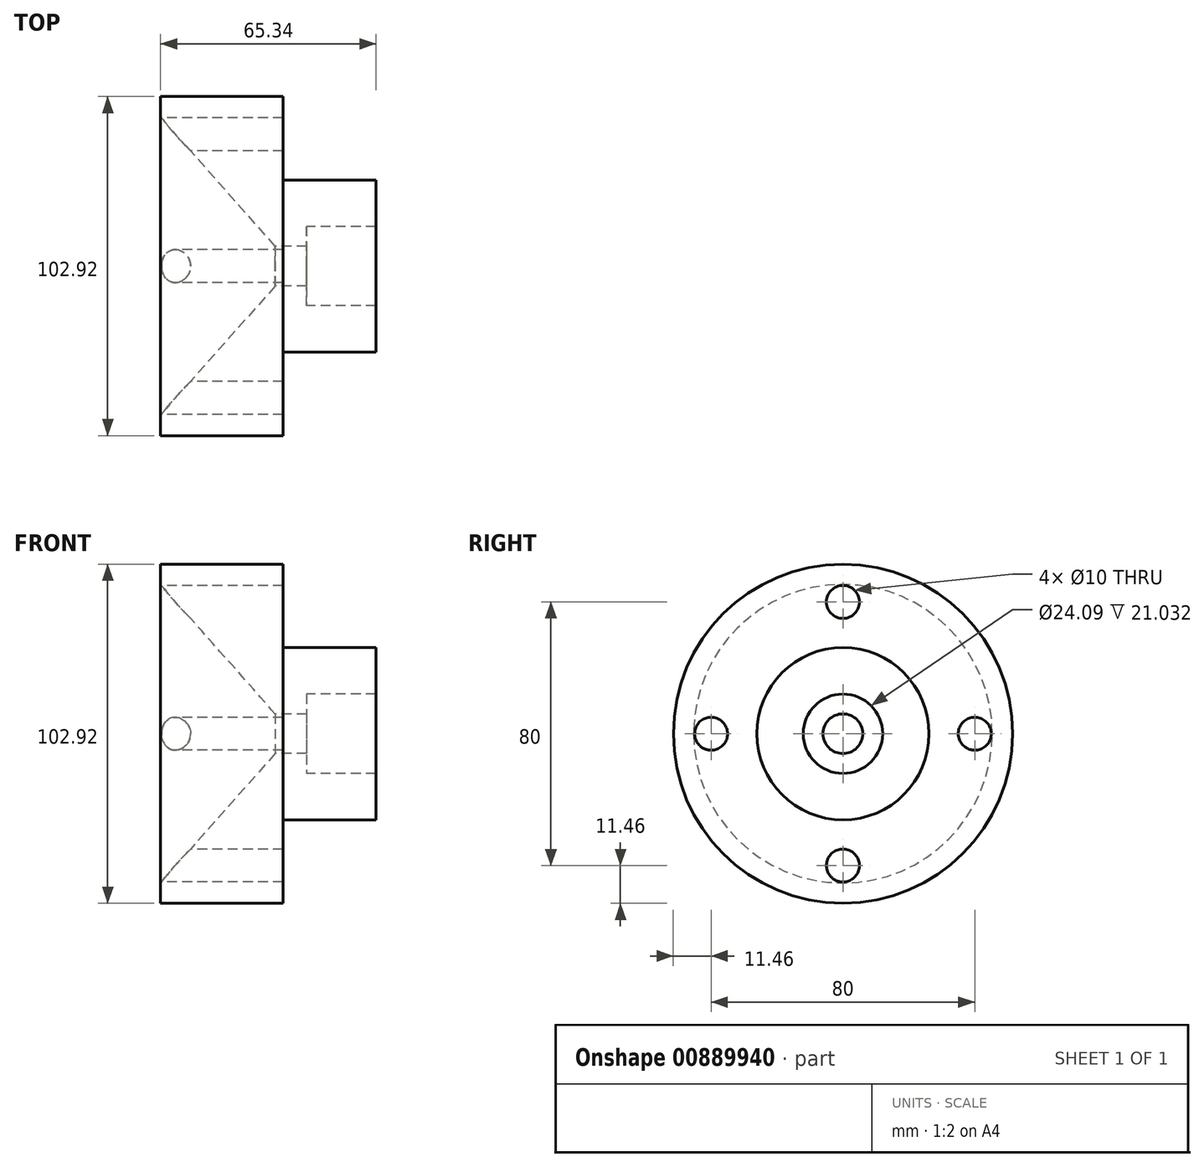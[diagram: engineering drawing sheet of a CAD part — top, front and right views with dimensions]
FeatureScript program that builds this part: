
annotation { "Feature Type Name" : "Feature", "Feature Type Description" : "" }
export const myFeature = defineFeature(function(context is Context, id is Id, definition is map)
    precondition{}
    {
        {
            var Q0;
            Q0=qCreatedBy(makeId("Front.planeOp"),FACE);
            var sketch = newSketch(context, id + "F0", { "sketchPlane" : qUnion([Q0])});
            skLineSegment(sketch, "E0", {"start": v(0, 45.3) * mm, "end": v(0, 51.46) * mm});
            skLineSegment(sketch, "E1", {"start": v(0, 51.46) * mm, "end": v(37.16, 51.46) * mm});
            skLineSegment(sketch, "E2", {"start": v(37.16, 51.46) * mm, "end": v(37.16, 26.14) * mm});
            skLineSegment(sketch, "E3", {"start": v(37.16, 26.14) * mm, "end": v(65.34, 26.14) * mm});
            skLineSegment(sketch, "E4", {"start": v(65.34, 26.14) * mm, "end": v(65.34, 12.05) * mm});
            skLineSegment(sketch, "E5", {"start": v(65.34, 12.05) * mm, "end": v(44.3, 12.05) * mm});
            skLineSegment(sketch, "E6", {"start": v(44.3, 12.05) * mm, "end": v(44.3, 6.02) * mm});
            skLineSegment(sketch, "E7", {"start": v(44.3, 6.02) * mm, "end": v(34.77, 6.02) * mm});
            skLineSegment(sketch, "E8", {"start": v(34.77, 6.02) * mm, "end": v(0, 45.3) * mm});
            skPoint(sketch, "E9.start.orphan", {"position": v(44.3, 0) * mm});
            skLineSegment(sketch, "E10", {"start": v(0, 0) * mm, "end": v(44.3, 0) * mm});
            skSolve(sketch);
        }
        {
            var Q0;
            Q0=makeQuery(id+"F0.imprint","IMPRINT",FACE,{"disambiguationData":[TD([[makeQuery(id+"F0.imprint","IMPRINT",EDGE,{"derivedFrom":sQuery(id+"F0.wireOp",EDGE,"E0")}),-1.0]])]});
            var Q1;
            Q1=sQuery(id+"F0.wireOp",EDGE,"E10");
            revolve(context, id + "F1", {"surfaceOperationType" : NewSurfaceOperationType.NEW, "entities" : qUnion([Q0]), "axis" : qUnion([Q1]), "revolveType" : RevolveType.FULL});
        }
        {
            var Q0;
            Q0=qCreatedBy(makeId("Right.planeOp"),FACE);
            var sketch = newSketch(context, id + "F2", { "sketchPlane" : qUnion([Q0])});
            skCircle(sketch, "E11", {"center": v(0, 40) * mm, "radius": 5 * mm});
            skCircle(sketch, "E12", {"center": v(-40, 0) * mm, "radius": 5 * mm});
            skCircle(sketch, "E13", {"center": v(40, 0) * mm, "radius": 5 * mm});
            skCircle(sketch, "E14", {"center": v(0, -40) * mm, "radius": 5 * mm});
            skSolve(sketch);
        }
        {
            var Q0;
            Q0 = qSketchRegion(id + "F2", true);
            extrude(context, id + "F3", {"entities" : qUnion([Q0]), "operationType" : NewBodyOperationType.REMOVE, "endBound" : BoundingType.THROUGH_ALL, "depth" : 25 * mm, "offsetDistance" : 25 * mm});
        }
    });
